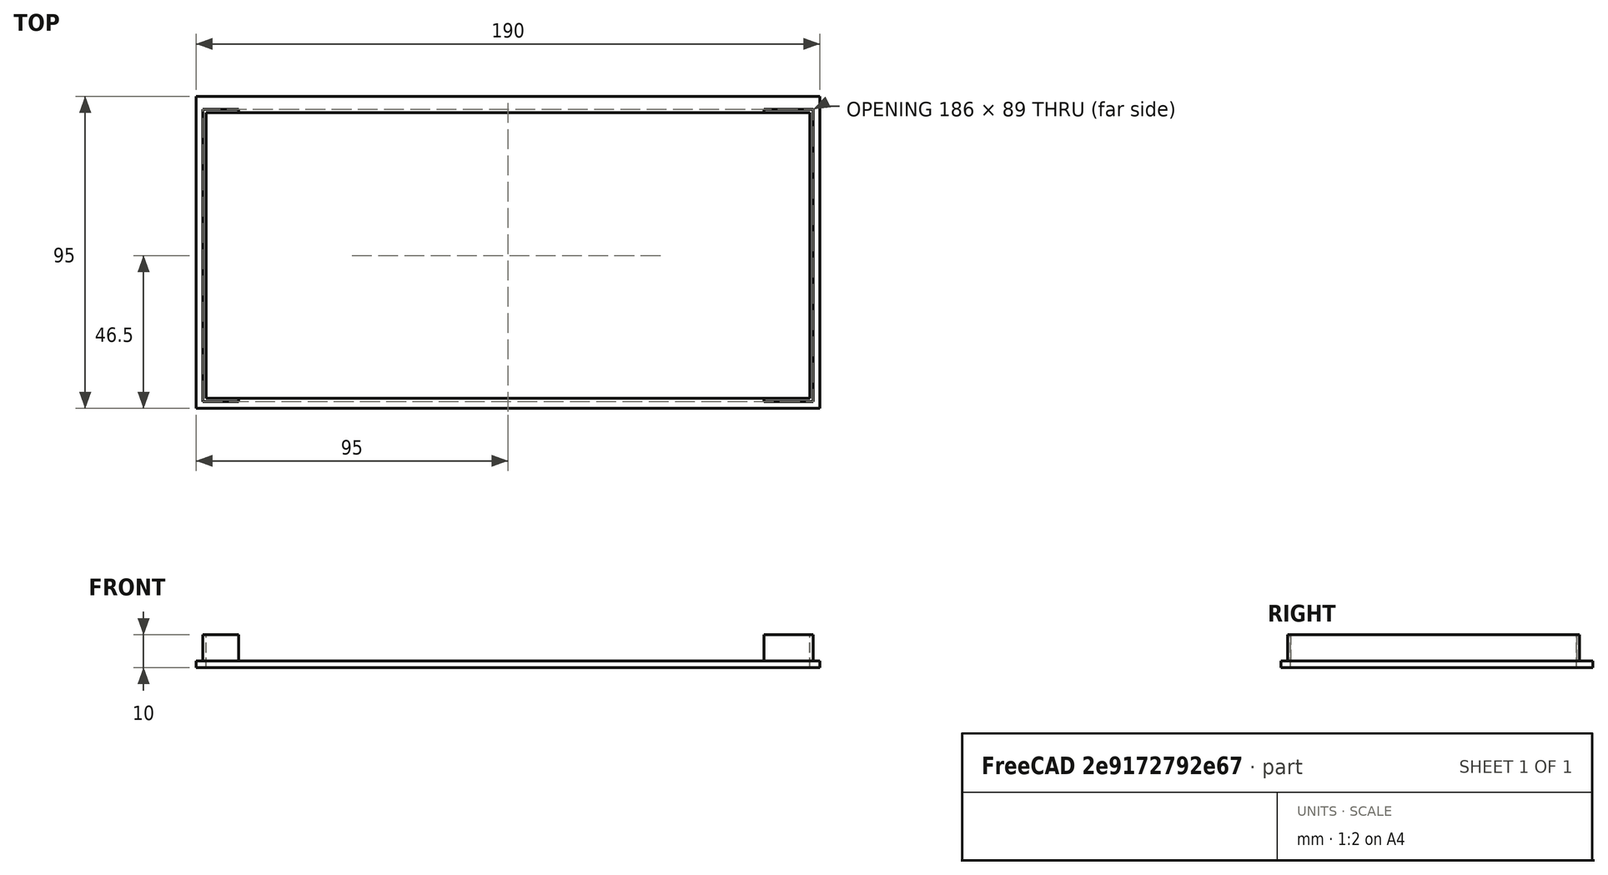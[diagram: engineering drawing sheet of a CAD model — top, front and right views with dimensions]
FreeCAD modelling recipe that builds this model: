
FCSTD DOCUMENT  (FreeCAD 0.20R29603 (Git))
Label: template1
License: All rights reserved
LicenseURL: http://en.wikipedia.org/wiki/All_rights_reserved
objects: PartDesign::AdditiveBox×2, PartDesign::SubtractiveBox×2, PartDesign::Body×1
note: 9 computed .brp shape members not serialized (recipe doc carries the construction recipe); baked Part::Feature solids carry a one-line shape summary decoded from their .brp

FEATURE [PartDesign::AdditiveBox] Box
  AttacherType = Attacher::AttachEngine3D
  Height = 2
  Length = 190
  MapMode = 5
  Support = -> [XY_Plane]
  Width = 95
FEATURE [PartDesign::AdditiveBox] Box001
  AttacherType = Attacher::AttachEngine3D
  AttachmentOffset = pos=(2,2,-2) rot=(0,0,1;0rad)
  BaseFeature = -> Box
  Height = 10
  Length = 186
  MapMode = 5
  Placement = pos=(2,2,0) rot=(0,0,1;0rad)
  Support = -> [Box]
  Width = 89
FEATURE [PartDesign::SubtractiveBox] Box002
  AttacherType = Attacher::AttachEngine3D
  AttachmentOffset = pos=(1,1,-2) rot=(0,0,1;0rad)
  BaseFeature = -> Box001
  Height = 10
  Length = 184
  MapMode = 5
  Placement = pos=(3,3,0) rot=(0,0,1;0rad)
  Support = -> [Box001]
  Width = 87
FEATURE [PartDesign::SubtractiveBox] Box003
  AttacherType = Attacher::AttachEngine3D
  AttachmentOffset = pos=(10,-1,0) rot=(0,0,1;0rad)
  BaseFeature = -> Box002
  Height = 10
  Length = 160
  MapMode = 5
  Placement = pos=(13,2,2) rot=(0,0,1;0rad)
  Support = -> [Box002]
  Width = 89
FEATURE [PartDesign::Body] Body
  Group = -> [Box,Box001,Box002,Box003]
  Origin = -> Origin
  Tip = -> Box003
